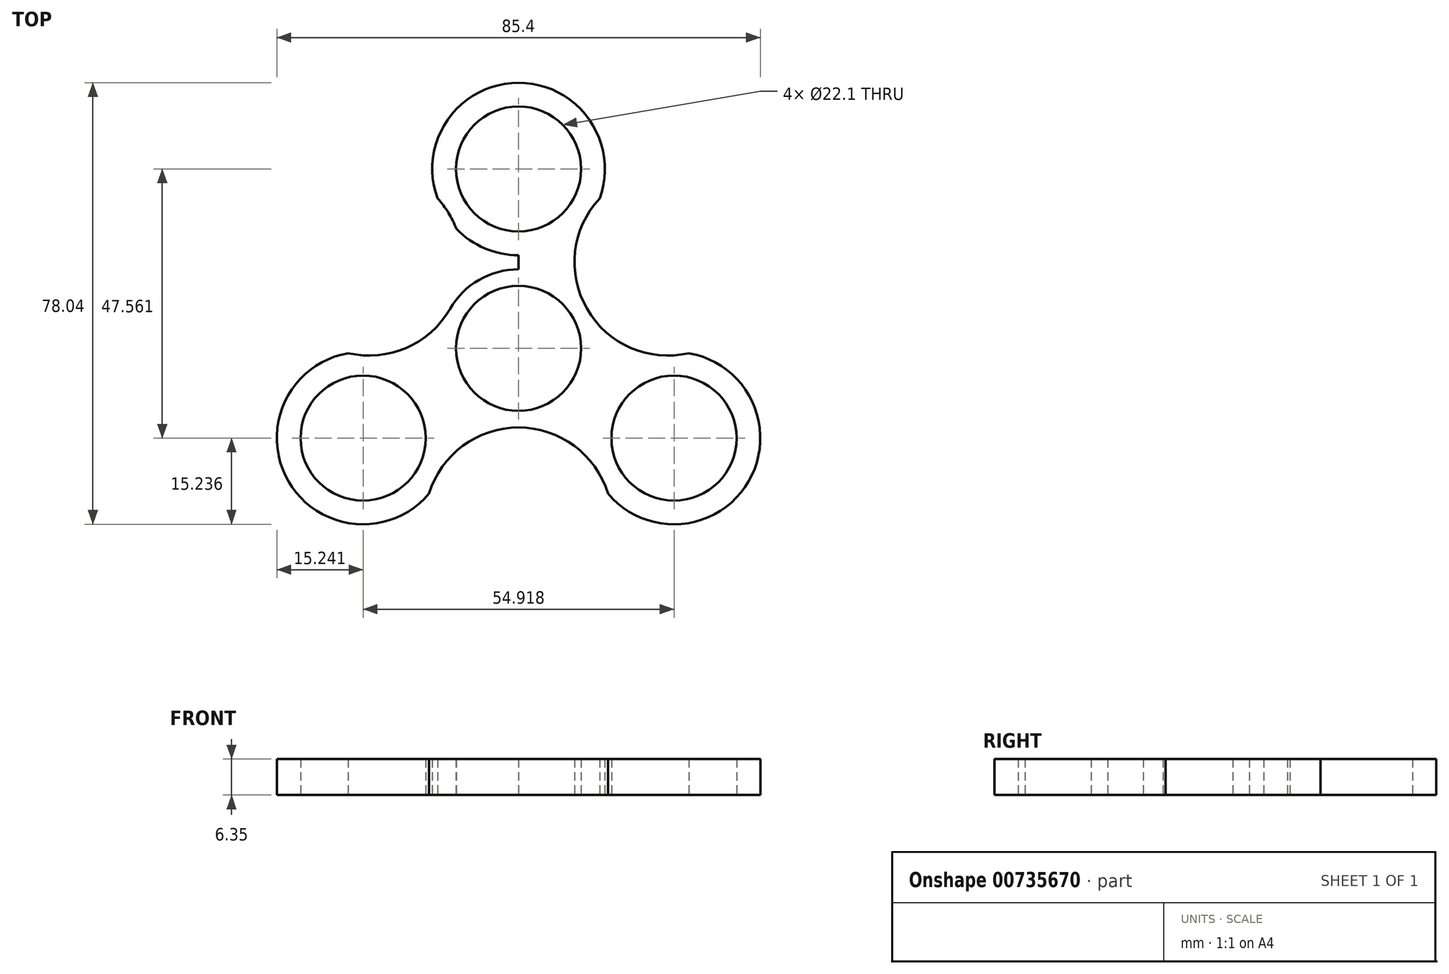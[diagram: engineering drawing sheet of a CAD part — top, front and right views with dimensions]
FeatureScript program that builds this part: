
annotation { "Feature Type Name" : "Feature", "Feature Type Description" : "" }
export const myFeature = defineFeature(function(context is Context, id is Id, definition is map)
    precondition{}
    {
        {
            var Q0;
            Q0=qCreatedBy(makeId("Top.planeOp"),FACE);
            var sketch = newSketch(context, id + "F0", { "sketchPlane" : qUnion([Q0])});
            skCircle(sketch, "E0", {"center": v(0, 0) * mm, "radius": 11.05 * mm});
            skCircle(sketch, "E1", {"center": v(0, 0) * mm, "radius": 13.97 * mm});
            skCircle(sketch, "E2", {"center": v(0, 31.7) * mm, "radius": 11.05 * mm});
            skCircle(sketch, "E3", {"center": v(0, 31.7) * mm, "radius": 15.24 * mm});
            skCircle(sketch, "E4.1.0", {"center": v(-27.46, -15.85) * mm, "radius": 11.05 * mm});
            skCircle(sketch, "E4.1.1", {"center": v(-27.46, -15.85) * mm, "radius": 15.24 * mm});
            skCircle(sketch, "E4.2.0", {"center": v(27.46, -15.85) * mm, "radius": 11.05 * mm});
            skCircle(sketch, "E4.2.1", {"center": v(27.46, -15.85) * mm, "radius": 15.24 * mm});
            skLineSegment(sketch, "E5", {"start": v(0, 0) * mm, "end": v(-26.4, 15.24) * mm});
            skLineSegment(sketch, "E6", {"start": v(0, 0) * mm, "end": v(0, 30.48) * mm});
            skArc(sketch, "E7", {"start": v(-30.11, -0.85) * mm, "mid": v(-12.1, 6.98) * mm, "end": v(-14.32, 26.5) * mm});
            skArc(sketch, "E8.1.0", {"start": v(15.79, -25.66) * mm, "mid": v(0, -13.97) * mm, "end": v(-15.79, -25.66) * mm});
            skArc(sketch, "E8.2.0", {"start": v(14.32, 26.5) * mm, "mid": v(12.1, 6.99) * mm, "end": v(30.11, -0.85) * mm});
            skSolve(sketch);
        }
        {
            var Q0;
            Q0=makeQuery(id+"F0.imprint","IMPRINT",FACE,{"disambiguationData":[TD([[makeQuery(id+"F0.imprint","IMPRINT",EDGE,{"derivedFrom":sQuery(id+"F0.wireOp",EDGE,"E2")}),-1.0]])]});
            var Q1;
            {var subQ0=sQuery(id+"F0.wireOp",EDGE,"E5");var subQ1=sQuery(id+"F0.wireOp",EDGE,"E0");var subQ2=makeQuery(id+"F0.imprint","INTERSECT",VERTEX,{"derivedFrom":[subQ1,subQ0]});Q1=makeQuery(id+"F0.imprint","IMPRINT",FACE,{"disambiguationData":[TD([[makeQuery(id+"F0.imprint","IMPRINT",EDGE,{"disambiguationData":[TD([[subQ2,1.0]])],"derivedFrom":subQ1}),-1.0]])]});}
            var Q2;
            {var subQ3=sQuery(id+"F0.wireOp",EDGE,"E7");var subQ5=sQuery(id+"F0.wireOp",EDGE,"E3");var subQ6=makeQuery(id+"F0.imprint","INTERSECT",VERTEX,{"disambiguationData":[OD(1.0)],"derivedFrom":[subQ5,subQ3]});Q2=makeQuery(id+"F0.imprint","IMPRINT",FACE,{"disambiguationData":[TD([[makeQuery(id+"F0.imprint","IMPRINT",EDGE,{"disambiguationData":[TD([[subQ6,-1.0]])],"derivedFrom":subQ5}),-1.0]])]});}
            var Q3;
            {var subQ0=sQuery(id+"F0.wireOp",EDGE,"E8.2.0");var subQ1=sQuery(id+"F0.wireOp",EDGE,"E1");var subQ2=makeQuery(id+"F0.imprint","INTERSECT",VERTEX,{"derivedFrom":[subQ1,subQ0]});Q3=makeQuery(id+"F0.imprint","IMPRINT",FACE,{"disambiguationData":[TD([[makeQuery(id+"F0.imprint","IMPRINT",EDGE,{"disambiguationData":[TD([[subQ2,-1.0]])],"derivedFrom":subQ1}),-1.0]])]});}
            var Q4;
            {var subQ3=sQuery(id+"F0.wireOp",EDGE,"E5");var subQ7=sQuery(id+"F0.wireOp",EDGE,"E0");var subQ8=makeQuery(id+"F0.imprint","INTERSECT",VERTEX,{"derivedFrom":[subQ7,subQ3]});Q4=makeQuery(id+"F0.imprint","IMPRINT",FACE,{"disambiguationData":[TD([[makeQuery(id+"F0.imprint","IMPRINT",EDGE,{"disambiguationData":[TD([[subQ8,-1.0]])],"derivedFrom":subQ7}),-1.0]])]});}
            var Q5;
            Q5=makeQuery(id+"F0.imprint","IMPRINT",FACE,{"disambiguationData":[TD([[makeQuery(id+"F0.imprint","IMPRINT",EDGE,{"derivedFrom":sQuery(id+"F0.wireOp",EDGE,"E4.2.0")}),-1.0]])]});
            var Q6;
            {var subQ0=sQuery(id+"F0.wireOp",EDGE,"E8.2.0");var subQ1=sQuery(id+"F0.wireOp",EDGE,"E1");var subQ2=makeQuery(id+"F0.imprint","INTERSECT",VERTEX,{"derivedFrom":[subQ1,subQ0]});Q6=makeQuery(id+"F0.imprint","IMPRINT",FACE,{"disambiguationData":[TD([[makeQuery(id+"F0.imprint","IMPRINT",EDGE,{"disambiguationData":[TD([[subQ2,1.0]])],"derivedFrom":subQ1}),-1.0]])]});}
            var Q7;
            {var subQ0=sQuery(id+"F0.wireOp",EDGE,"E8.1.0");var subQ5=sQuery(id+"F0.wireOp",EDGE,"E4.1.1");var subQ6=makeQuery(id+"F0.imprint","INTERSECT",VERTEX,{"disambiguationData":[OD(1.0)],"derivedFrom":[subQ5,subQ0]});Q7=makeQuery(id+"F0.imprint","IMPRINT",FACE,{"disambiguationData":[TD([[makeQuery(id+"F0.imprint","IMPRINT",EDGE,{"disambiguationData":[TD([[subQ6,-1.0]])],"derivedFrom":subQ5}),-1.0]])]});}
            var Q8;
            Q8=makeQuery(id+"F0.imprint","IMPRINT",FACE,{"disambiguationData":[TD([[makeQuery(id+"F0.imprint","IMPRINT",EDGE,{"derivedFrom":sQuery(id+"F0.wireOp",EDGE,"E4.1.0")}),-1.0]])]});
            extrude(context, id + "F1", {"entities" : qUnion([Q0, Q1, Q2, Q3, Q4, Q5, Q6, Q7, Q8]), "depth" : 6.35 * mm, "offsetDistance" : 25.4 * mm});
        }
    });
